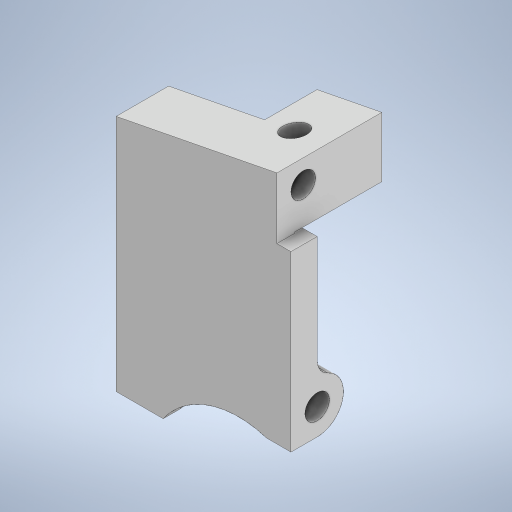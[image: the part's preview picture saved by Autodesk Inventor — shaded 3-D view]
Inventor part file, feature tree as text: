
AUTODESK INVENTOR PART (.ipt)
format: ipt  version: 2023.5 (Build 275446000, 446)  size: 365,056 bytes
history: native  units: mm
features: reference x12, sketch x11, projected_geometry x10, other x9, extrude x8, hole x3, fillet x1
ambient origin geometry x8: Origin, YZ Plane, XZ Plane, XY Plane, X Axis, Y Axis, Z Axis, Center Point
bodies: Body1 (feature_tree)
feature tree (54):
  other  "Bryła1"
  extrude  "Wyciągnięcie proste1"  Depth=2.0mm TaperAngle=0.0deg
  extrude  "Wyciągnięcie proste2"  Depth=5.0mm TaperAngle=0.0deg
  extrude  "Wyciągnięcie proste3"  Depth=4.0mm TaperAngle=0.0deg
  extrude  "Wyciągnięcie proste4"  Depth=6.0mm TaperAngle=0.0deg
  extrude  "Wyciągnięcie proste5"  Depth=1.0mm TaperAngle=0.0deg
  hole  "Otwór1"  [1 undecoded]
  extrude  "Wyciągnięcie proste6"  Depth=6.0mm
  hole  "Otwór2"  [1 undecoded]
  hole  "Otwór3"  [1 undecoded]
  extrude  "Wyciągnięcie proste7"  Depth=6.0mm
  extrude  "Wyciągnięcie proste8"  TaperAngle=0.0deg  [1 undecoded]
  fillet  "Zaokrąglenie1"  Radius=1.0mm
  sketch  "Szkic1"
  reference  "Odniesienie1"
  reference  "Odniesienie2"
  reference  "Odniesienie3"
  reference  "Odniesienie4"
  reference  "Odniesienie5"
  sketch  "Szkic2"
  reference  "Odniesienie6"
  projected_geometry  "Pętla rzutowana1"
  sketch  "Szkic3"
  reference  "Odniesienie7"
  reference  "Odniesienie8"
  projected_geometry  "Pętla rzutowana2"
  sketch  "Szkic4"
  projected_geometry  "Pętla rzutowana3"
  reference  "Odniesienie9"
  sketch  "Szkic5"
  projected_geometry  "Pętla rzutowana4"
  projected_geometry  "Pętla rzutowana5"
  sketch  "Szkic6"
  projected_geometry  "Pętla rzutowana6"
  sketch  "Szkic7"
  projected_geometry  "Pętla rzutowana7"
  sketch  "Szkic8"
  projected_geometry  "Pętla rzutowana8"
  sketch  "Szkic9"
  reference  "Odniesienie10"
  sketch  "Szkic10"
  projected_geometry  "Pętla rzutowana9"
  reference  "Odniesienie11"
  reference  "Odniesienie12"
  sketch  "Szkic11"
  projected_geometry  "Pętla rzutowana10"
  parser-record x1  (decoder bookkeeping rows leaked as tree rows — omitted from the tree; the rows remain in map.json)
  other  "stratos_v2_mechanics.iam"
  other  "nozzyk:1"
  other  "podstawa_v2:1"
  other  "montaz_osi:1"
  other  "MikroSumo:1"
  other  "lipo-300:1"
  other  "pcb_dolne:1"
note: 4 required parameter values undecoded (feature->parameter linkage not recoverable at this tier; creation-order binding heuristic only, values carry confidence <= 0.55)
note: 1 file-system path scrubbed to <path> (originals preserved in map.json)
